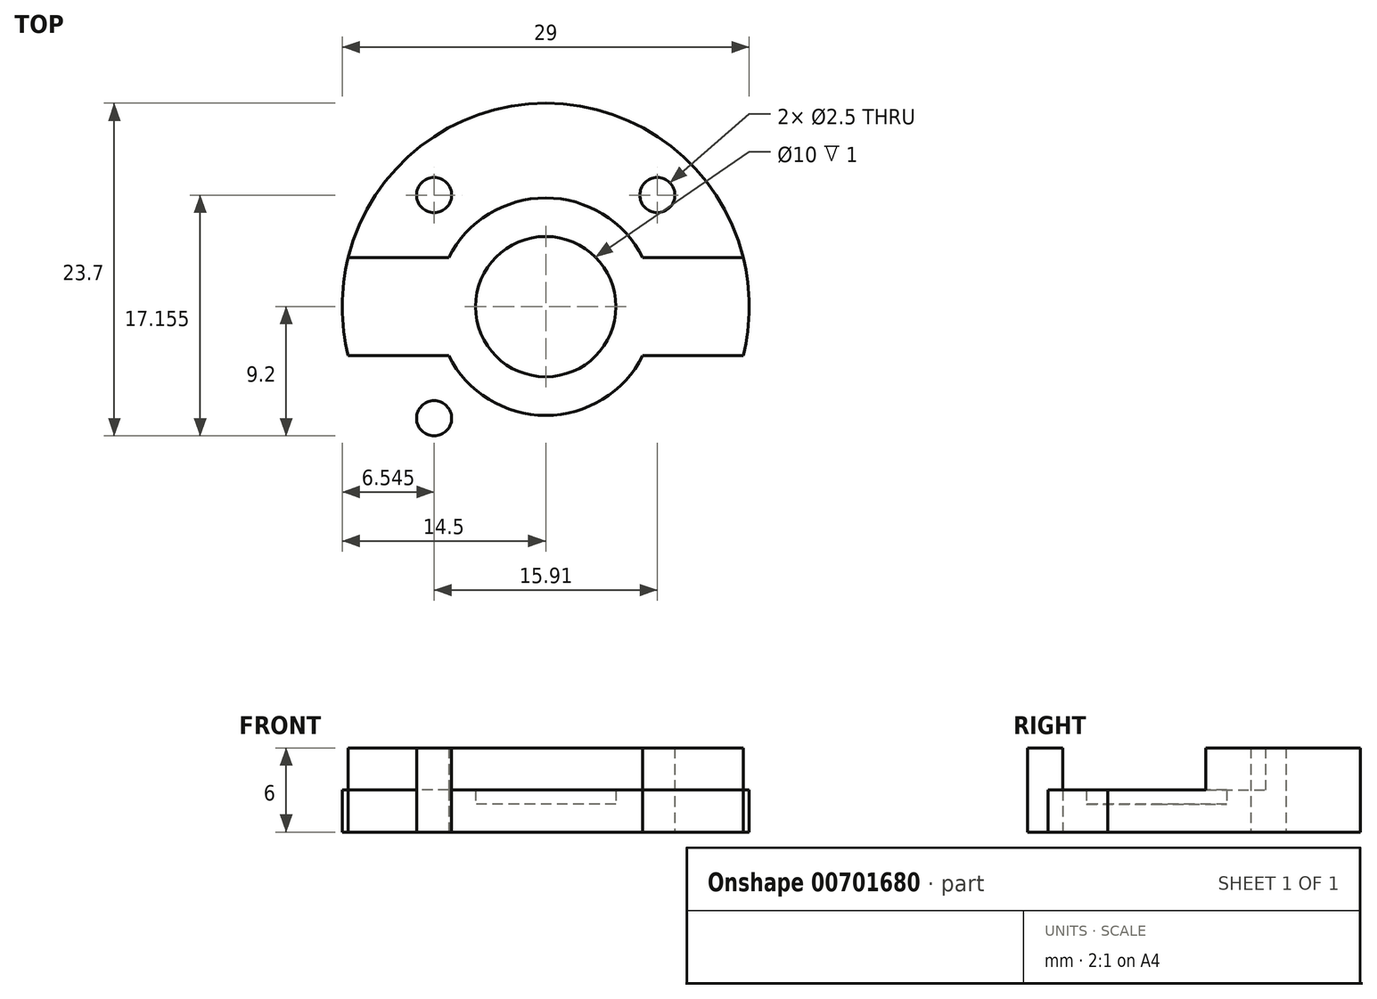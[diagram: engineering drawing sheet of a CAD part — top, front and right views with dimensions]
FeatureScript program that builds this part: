
annotation { "Feature Type Name" : "Feature", "Feature Type Description" : "" }
export const myFeature = defineFeature(function(context is Context, id is Id, definition is map)
    precondition{}
    {
        {
            var Q0;
            Q0=qCreatedBy(makeId("Top.planeOp"),FACE);
            var sketch = newSketch(context, id + "F0", { "sketchPlane" : qUnion([Q0])});
            skCircle(sketch, "E0", {"center": v(0, 0) * mm, "radius": 14.5 * mm});
            skLineSegment(sketch, "E1", {"start": v(0, 0) * mm, "end": v(-17.97, 17.97) * mm, "construction": true});
            skCircle(sketch, "E2", {"center": v(-7.95, 7.95) * mm, "radius": 1.25 * mm});
            skCircle(sketch, "E3.MirrorC", {"center": v(7.95, 7.95) * mm, "radius": 1.25 * mm});
            skCircle(sketch, "E4.MirrorC", {"center": v(-7.95, -7.95) * mm, "radius": 1.25 * mm});
            skCircle(sketch, "E5.MirrorC", {"center": v(7.95, -7.95) * mm, "radius": 1.25 * mm});
            skCircle(sketch, "E6", {"center": v(0, 0) * mm, "radius": 7.75 * mm});
            skCircle(sketch, "E7", {"center": v(0, 0) * mm, "radius": 5 * mm});
            skLineSegment(sketch, "E8", {"start": v(6.91, 3.5) * mm, "end": v(14.07, 3.5) * mm});
            skLineSegment(sketch, "E9.MirrorCS", {"start": v(6.91, -3.5) * mm, "end": v(14.07, -3.5) * mm});
            skLineSegment(sketch, "E10.MirrorCS", {"start": v(-6.91, 3.5) * mm, "end": v(-14.07, 3.5) * mm});
            skLineSegment(sketch, "E11.MirrorCS", {"start": v(-6.91, -3.5) * mm, "end": v(-14.07, -3.5) * mm});
            skArc(sketch, "E12", {"start": v(-6.91, 3.5) * mm, "mid": v(0, 7.75) * mm, "end": v(6.91, 3.5) * mm});
            skArc(sketch, "E13", {"start": v(-14.07, 3.5) * mm, "mid": v(0, 14.5) * mm, "end": v(14.07, 3.5) * mm});
            skArc(sketch, "E14", {"start": v(-6.91, -3.5) * mm, "mid": v(0, -7.75) * mm, "end": v(6.91, -3.5) * mm});
            skArc(sketch, "E15", {"start": v(-14.07, -3.5) * mm, "mid": v(0, -14.5) * mm, "end": v(14.07, -3.5) * mm});
            skSolve(sketch);
        }
        {
            assignVariable(context, id + "F1", {"name" : "z0", "anyValue" : 3 * mm});
        }
        {
            var Q0;
            {var subQ0=sQuery(id+"F0.wireOp",EDGE,"E10.MirrorCS");Q0=makeQuery(id+"F0.imprint","IMPRINT",FACE,{"disambiguationData":[TD([[makeQuery(id+"F0.imprint","IMPRINT",EDGE,{"derivedFrom":subQ0}),1.0]])]});}
            var Q1;
            Q1=makeQuery(id+"F0.imprint","IMPRINT",FACE,{"disambiguationData":[TD([[makeQuery(id+"F0.imprint","IMPRINT",EDGE,{"derivedFrom":sQuery(id+"F0.wireOp",EDGE,"E7")}),-1.0]])]});
            var Q2;
            {var subQ0=sQuery(id+"F0.wireOp",EDGE,"E8");Q2=makeQuery(id+"F0.imprint","IMPRINT",FACE,{"disambiguationData":[TD([[makeQuery(id+"F0.imprint","IMPRINT",EDGE,{"derivedFrom":subQ0}),-1.0]])]});}
            extrude(context, id + "F2", {"entities" : qUnion([Q0, Q1, Q2]), "depth" : getVariable(context, 'z0'), "offsetDistance" : 25 * mm});
        }
        {
            var Q0;
            Q0=makeQuery(id+"F0.imprint","IMPRINT",FACE,{"disambiguationData":[TD([[makeQuery(id+"F0.imprint","IMPRINT",EDGE,{"derivedFrom":sQuery(id+"F0.wireOp",EDGE,"E2")}),-1.0]])]});
            var Q1;
            Q1=makeQuery(id+"F0.imprint","IMPRINT",FACE,{"disambiguationData":[TD([[makeQuery(id+"F0.imprint","IMPRINT",EDGE,{"derivedFrom":sQuery(id+"F0.wireOp",EDGE,"E4.MirrorC")}),1.0]])]});
            extrude(context, id + "F3", {"entities" : qUnion([Q0, Q1]), "operationType" : NewBodyOperationType.ADD, "depth" : getVariable(context, 'z0') + 3 * mm, "offsetDistance" : 25 * mm});
        }
        {
            var Q0;
            Q0=makeQuery(id+"F0.imprint","IMPRINT",FACE,{"disambiguationData":[TD([[makeQuery(id+"F0.imprint","IMPRINT",EDGE,{"derivedFrom":sQuery(id+"F0.wireOp",EDGE,"E7")}),1.0]])]});
            extrude(context, id + "F4", {"entities" : qUnion([Q0]), "operationType" : NewBodyOperationType.ADD, "depth" : 2 * mm, "offsetDistance" : 25 * mm});
        }
    });
